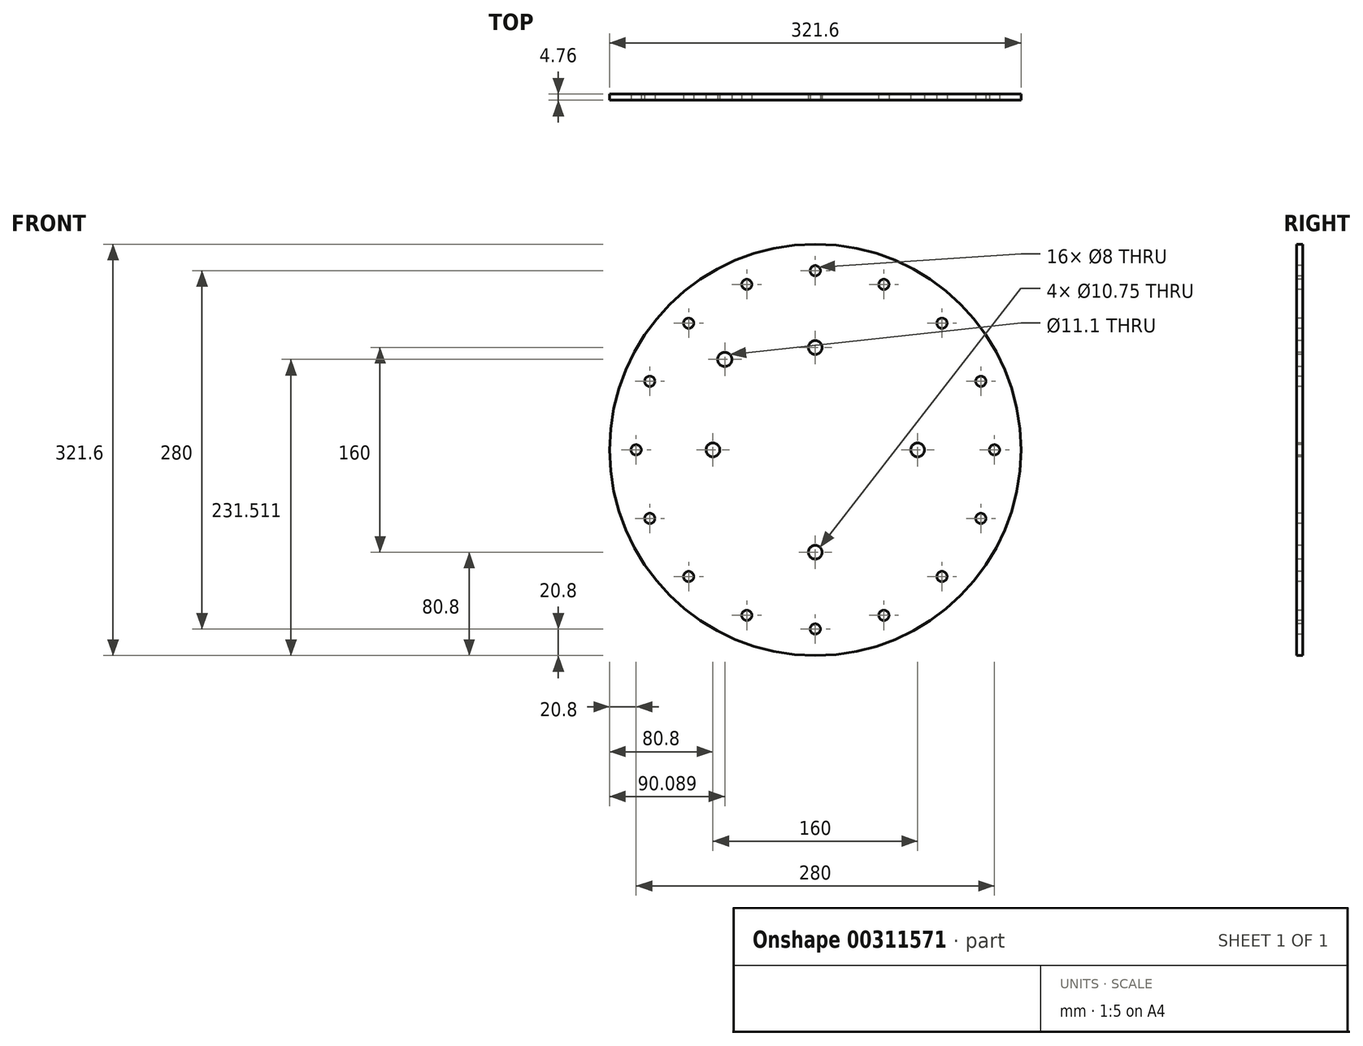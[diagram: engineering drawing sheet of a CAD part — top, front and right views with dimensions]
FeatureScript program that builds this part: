
annotation { "Feature Type Name" : "Feature", "Feature Type Description" : "" }
export const myFeature = defineFeature(function(context is Context, id is Id, definition is map)
    precondition{}
    {
        {
            var Q0;
            Q0=qCreatedBy(makeId("Front.planeOp"),FACE);
            var sketch = newSketch(context, id + "F0", { "sketchPlane" : qUnion([Q0])});
            skCircle(sketch, "E0", {"center": v(0, 0) * mm, "radius": 160.8 * mm});
            skSolve(sketch);
        }
        {
            var Q0;
            Q0=makeQuery(id+"F0.imprint","IMPRINT",FACE,{"disambiguationData":[TD([[makeQuery(id+"F0.imprint","IMPRINT",EDGE,{"derivedFrom":sQuery(id+"F0.wireOp",EDGE,"E0")}),1.0]])]});
            extrude(context, id + "F1", {"entities" : qUnion([Q0]), "depth" : 4.76 * mm});
        }
        {
            var Q0;
            Q0=makeQuery(id+"F1.opExtrude","CAP_FACE",FACE,{"disambiguationData":[OSD([sQuery(id+"F0.wireOp",EDGE,"E0")])],"isStart":false});
            var sketch = newSketch(context, id + "F2", { "sketchPlane" : qUnion([Q0])});
            skPoint(sketch, "E1", {"position": v(0, 80) * mm});
            skPoint(sketch, "E2", {"position": v(0, -80) * mm});
            skPoint(sketch, "E3", {"position": v(80, 0) * mm});
            skPoint(sketch, "E4", {"position": v(-80, 0) * mm});
            skPoint(sketch, "E5", {"position": v(0, 0) * mm});
            skSolve(sketch);
        }
        {
            var Q0;
            Q0=sQuery(id+"F2.wireOp",VERTEX,"E4");
            var Q1;
            Q1=sQuery(id+"F2.wireOp",VERTEX,"E1");
            var Q2;
            Q2=sQuery(id+"F2.wireOp",VERTEX,"E3");
            var Q3;
            Q3=sQuery(id+"F2.wireOp",VERTEX,"E2");
            var Q4;
            Q4=makeQuery(id+"F1.opExtrude","SWEPT_BODY",BODY,{"disambiguationData":[OSD([sQuery(id+"F0.wireOp",EDGE,"E0")])]});
            hole(context, id + "F3", {"style" : HoleStyle.SIMPLE, "endStyle" : HoleEndStyle.THROUGH, "holeDiameter" : 10.75 * mm, "tappedDepth" : 12 * mm, "tapClearance" : 3, "locations" : qUnion([Q0, Q1, Q2, Q3]), "scope" : qUnion([Q4])});
        }
        {
            var Q0;
            Q0=makeQuery(id+"F1.opExtrude","CAP_FACE",FACE,{"disambiguationData":[OSD([sQuery(id+"F0.wireOp",EDGE,"E0")])],"isStart":false});
            var sketch = newSketch(context, id + "F4", { "sketchPlane" : qUnion([Q0])});
            skCircle(sketch, "E6", {"center": v(0, 0) * mm, "radius": 140 * mm});
            skPoint(sketch, "E7", {"position": v(0, 140) * mm});
            skPoint(sketch, "E8.1.0", {"position": v(53.58, 129.34) * mm});
            skPoint(sketch, "E8.2.0", {"position": v(99, 99) * mm});
            skPoint(sketch, "E8.3.0", {"position": v(129.34, 53.58) * mm});
            skPoint(sketch, "E8.4.0", {"position": v(140, 0) * mm});
            skLineSegment(sketch, "E8.anchor1", {"start": v(0, 0) * mm, "end": v(0, 140) * mm, "construction": true});
            skLineSegment(sketch, "E8.anchor2", {"start": v(0, 0) * mm, "end": v(140, 0) * mm, "construction": true});
            skPoint(sketch, "E9.1.0", {"position": v(129.34, -53.58) * mm});
            skPoint(sketch, "E9.2.0", {"position": v(99, -99) * mm});
            skPoint(sketch, "E9.3.0", {"position": v(53.58, -129.34) * mm});
            skPoint(sketch, "E9.4.0", {"position": v(0, -140) * mm});
            skLineSegment(sketch, "E9.anchor2", {"start": v(0, 0) * mm, "end": v(0, -140) * mm, "construction": true});
            skPoint(sketch, "E10.1.0", {"position": v(-53.58, -129.34) * mm});
            skPoint(sketch, "E10.2.0", {"position": v(-99, -99) * mm});
            skPoint(sketch, "E10.3.0", {"position": v(-129.34, -53.58) * mm});
            skPoint(sketch, "E10.4.0", {"position": v(-140, 0) * mm});
            skLineSegment(sketch, "E10.anchor2", {"start": v(0, 0) * mm, "end": v(-140, 0) * mm, "construction": true});
            skPoint(sketch, "E11.1.0", {"position": v(-129.34, 53.58) * mm});
            skPoint(sketch, "E11.2.0", {"position": v(-99, 99) * mm});
            skPoint(sketch, "E11.3.0", {"position": v(-53.58, 129.34) * mm});
            skPoint(sketch, "E12", {"position": v(-74.25, 74.25) * mm});
            skSolve(sketch);
        }
        {
            var Q0;
            Q0=sQuery(id+"F4.wireOp",VERTEX,"E11.3.0");
            var Q1;
            Q1=sQuery(id+"F4.wireOp",VERTEX,"E7");
            var Q2;
            Q2=sQuery(id+"F4.wireOp",VERTEX,"E8.1.0");
            var Q3;
            Q3=sQuery(id+"F4.wireOp",VERTEX,"E8.2.0");
            var Q4;
            Q4=sQuery(id+"F4.wireOp",VERTEX,"E8.3.0");
            var Q5;
            Q5=sQuery(id+"F4.wireOp",VERTEX,"E8.4.0");
            var Q6;
            Q6=sQuery(id+"F4.wireOp",VERTEX,"E9.1.0");
            var Q7;
            Q7=sQuery(id+"F4.wireOp",VERTEX,"E9.2.0");
            var Q8;
            Q8=sQuery(id+"F4.wireOp",VERTEX,"E9.3.0");
            var Q9;
            Q9=sQuery(id+"F4.wireOp",VERTEX,"E9.4.0");
            var Q10;
            Q10=sQuery(id+"F4.wireOp",VERTEX,"E10.1.0");
            var Q11;
            Q11=sQuery(id+"F4.wireOp",VERTEX,"E10.2.0");
            var Q12;
            Q12=sQuery(id+"F4.wireOp",VERTEX,"E10.3.0");
            var Q13;
            Q13=sQuery(id+"F4.wireOp",VERTEX,"E10.4.0");
            var Q14;
            Q14=sQuery(id+"F4.wireOp",VERTEX,"E11.1.0");
            var Q15;
            Q15=sQuery(id+"F4.wireOp",VERTEX,"E11.2.0");
            var Q16;
            Q16=makeQuery(id+"F1.opExtrude","SWEPT_BODY",BODY,{"disambiguationData":[OSD([sQuery(id+"F0.wireOp",EDGE,"E0")])]});
            hole(context, id + "F5", {"style" : HoleStyle.SIMPLE, "endStyle" : HoleEndStyle.THROUGH, "holeDiameter" : 8 * mm, "tappedDepth" : 12 * mm, "tapClearance" : 3, "locations" : qUnion([Q0, Q1, Q2, Q3, Q4, Q5, Q6, Q7, Q8, Q9, Q10, Q11, Q12, Q13, Q14, Q15]), "scope" : qUnion([Q16])});
        }
        {
            var Q0;
            Q0=makeQuery(id+"F1.opExtrude","CAP_FACE",FACE,{"disambiguationData":[OSD([sQuery(id+"F0.wireOp",EDGE,"E0")])],"isStart":false});
            var sketch = newSketch(context, id + "F6", { "sketchPlane" : qUnion([Q0])});
            skPoint(sketch, "E13", {"position": v(-70.71, 70.71) * mm});
            skPoint(sketch, "E14", {"position": v(0, 0) * mm});
            skSolve(sketch);
        }
        {
            var Q0;
            Q0=sQuery(id+"F6.wireOp",VERTEX,"E13");
            var Q1;
            Q1=makeQuery(id+"F1.opExtrude","SWEPT_BODY",BODY,{"disambiguationData":[OSD([sQuery(id+"F0.wireOp",EDGE,"E0")])]});
            hole(context, id + "F7", {"style" : HoleStyle.SIMPLE, "endStyle" : HoleEndStyle.THROUGH, "holeDiameter" : 11.1 * mm, "tappedDepth" : 12 * mm, "tapClearance" : 3, "locations" : qUnion([Q0]), "scope" : qUnion([Q1])});
        }
    });
